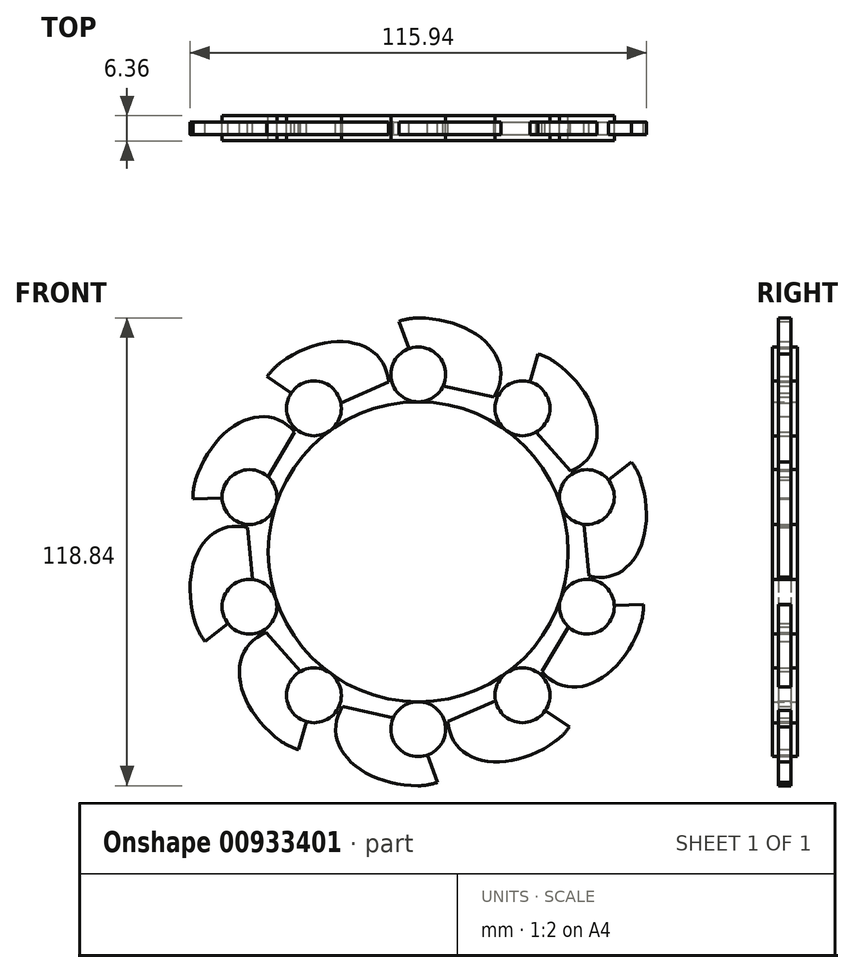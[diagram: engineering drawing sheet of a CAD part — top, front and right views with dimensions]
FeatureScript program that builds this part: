
annotation { "Feature Type Name" : "Feature", "Feature Type Description" : "" }
export const myFeature = defineFeature(function(context is Context, id is Id, definition is map)
    precondition{}
    {
        {
            var Q0;
            Q0=qCreatedBy(makeId("Front.planeOp"),FACE);
            var sketch = newSketch(context, id + "F0", { "sketchPlane" : qUnion([Q0])});
            skCircle(sketch, "E0", {"center": v(0, 0) * mm, "radius": 38.1 * mm});
            skCircle(sketch, "E1", {"center": v(0, 45.06) * mm, "radius": 6.96 * mm});
            skPoint(sketch, "E1.first.point", {"position": v(0.3, 38.1) * mm});
            skPoint(sketch, "E1.second.point", {"position": v(0, 52.02) * mm});
            skPoint(sketch, "E1.third.point", {"position": v(6.89, 46.1) * mm});
            skEllipticalArc(sketch, "E2", {});
            skArc(sketch, "E3", {"start": v(0, 59.42) * mm, "mid": v(-2.5, 59.2) * mm, "end": v(-4.91, 58.55) * mm});
            skPoint(sketch, "E3.second.point", {"position": v(0, 59.42) * mm});
            skLineSegment(sketch, "E4", {"start": v(19.23, 39.33) * mm, "end": v(6.33, 42.15) * mm});
            skLineSegment(sketch, "E5", {"start": v(-4.91, 58.55) * mm, "end": v(-2.38, 51.6) * mm});
            skEllipticalArc(sketch, "E6.1.0", {});
            skPoint(sketch, "E6.1.1", {"position": v(-34.93, 48.07) * mm});
            skLineSegment(sketch, "E6.1.2", {"start": v(-38.4, 44.48) * mm, "end": v(-32.26, 40.35) * mm});
            skArc(sketch, "E6.1.3", {"start": v(-34.93, 48.07) * mm, "mid": v(-36.82, 46.43) * mm, "end": v(-38.4, 44.48) * mm});
            skCircle(sketch, "E6.1.4", {"center": v(-26.49, 36.46) * mm, "radius": 6.96 * mm});
            skLineSegment(sketch, "E6.1.5", {"start": v(-7.56, 43.12) * mm, "end": v(-19.66, 37.82) * mm});
            skEllipticalArc(sketch, "E6.2.0", {});
            skPoint(sketch, "E6.2.1", {"position": v(-56.51, 18.36) * mm});
            skLineSegment(sketch, "E6.2.2", {"start": v(-57.2, 13.42) * mm, "end": v(-49.81, 13.68) * mm});
            skArc(sketch, "E6.2.3", {"start": v(-56.51, 18.36) * mm, "mid": v(-57.08, 15.92) * mm, "end": v(-57.2, 13.42) * mm});
            skCircle(sketch, "E6.2.4", {"center": v(-42.86, 13.92) * mm, "radius": 6.96 * mm});
            skLineSegment(sketch, "E6.2.5", {"start": v(-31.46, 30.44) * mm, "end": v(-38.14, 19.04) * mm});
            skEllipticalArc(sketch, "E6.3.0", {});
            skPoint(sketch, "E6.3.1", {"position": v(-56.51, -18.36) * mm});
            skLineSegment(sketch, "E6.3.2", {"start": v(-54.17, -22.77) * mm, "end": v(-48.34, -18.21) * mm});
            skArc(sketch, "E6.3.3", {"start": v(-56.51, -18.36) * mm, "mid": v(-55.53, -20.67) * mm, "end": v(-54.17, -22.77) * mm});
            skCircle(sketch, "E6.3.4", {"center": v(-42.86, -13.92) * mm, "radius": 6.96 * mm});
            skLineSegment(sketch, "E6.3.5", {"start": v(-43.35, 6.13) * mm, "end": v(-42.05, -7.01) * mm});
            skEllipticalArc(sketch, "E6.4.0", {});
            skPoint(sketch, "E6.4.1", {"position": v(-34.93, -48.07) * mm});
            skLineSegment(sketch, "E6.4.2", {"start": v(-30.44, -50.26) * mm, "end": v(-28.4, -43.15) * mm});
            skArc(sketch, "E6.4.3", {"start": v(-34.93, -48.07) * mm, "mid": v(-32.78, -49.36) * mm, "end": v(-30.44, -50.26) * mm});
            skCircle(sketch, "E6.4.4", {"center": v(-26.49, -36.46) * mm, "radius": 6.96 * mm});
            skLineSegment(sketch, "E6.4.5", {"start": v(-38.67, -20.52) * mm, "end": v(-29.9, -30.39) * mm});
            skEllipticalArc(sketch, "E6.5.0", {});
            skPoint(sketch, "E6.5.1", {"position": v(0, -59.42) * mm});
            skLineSegment(sketch, "E6.5.2", {"start": v(4.91, -58.55) * mm, "end": v(2.38, -51.6) * mm});
            skArc(sketch, "E6.5.3", {"start": v(0, -59.42) * mm, "mid": v(2.5, -59.2) * mm, "end": v(4.91, -58.55) * mm});
            skCircle(sketch, "E6.5.4", {"center": v(0, -45.06) * mm, "radius": 6.96 * mm});
            skLineSegment(sketch, "E6.5.5", {"start": v(-19.23, -39.33) * mm, "end": v(-6.33, -42.15) * mm});
            skEllipticalArc(sketch, "E6.6.0", {});
            skPoint(sketch, "E6.6.1", {"position": v(34.93, -48.07) * mm});
            skLineSegment(sketch, "E6.6.2", {"start": v(38.4, -44.48) * mm, "end": v(32.26, -40.35) * mm});
            skArc(sketch, "E6.6.3", {"start": v(34.93, -48.07) * mm, "mid": v(36.82, -46.43) * mm, "end": v(38.4, -44.48) * mm});
            skCircle(sketch, "E6.6.4", {"center": v(26.49, -36.46) * mm, "radius": 6.96 * mm});
            skLineSegment(sketch, "E6.6.5", {"start": v(7.56, -43.12) * mm, "end": v(19.66, -37.82) * mm});
            skEllipticalArc(sketch, "E6.7.0", {});
            skPoint(sketch, "E6.7.1", {"position": v(56.51, -18.36) * mm});
            skLineSegment(sketch, "E6.7.2", {"start": v(57.2, -13.42) * mm, "end": v(49.81, -13.68) * mm});
            skArc(sketch, "E6.7.3", {"start": v(56.51, -18.36) * mm, "mid": v(57.08, -15.92) * mm, "end": v(57.2, -13.42) * mm});
            skCircle(sketch, "E6.7.4", {"center": v(42.86, -13.92) * mm, "radius": 6.96 * mm});
            skLineSegment(sketch, "E6.7.5", {"start": v(31.46, -30.44) * mm, "end": v(38.14, -19.04) * mm});
            skEllipticalArc(sketch, "E6.8.0", {});
            skPoint(sketch, "E6.8.1", {"position": v(56.51, 18.36) * mm});
            skLineSegment(sketch, "E6.8.2", {"start": v(54.17, 22.77) * mm, "end": v(48.34, 18.21) * mm});
            skArc(sketch, "E6.8.3", {"start": v(56.51, 18.36) * mm, "mid": v(55.53, 20.67) * mm, "end": v(54.17, 22.77) * mm});
            skCircle(sketch, "E6.8.4", {"center": v(42.86, 13.92) * mm, "radius": 6.96 * mm});
            skLineSegment(sketch, "E6.8.5", {"start": v(43.35, -6.13) * mm, "end": v(42.05, 7.01) * mm});
            skEllipticalArc(sketch, "E6.9.0", {});
            skPoint(sketch, "E6.9.1", {"position": v(34.93, 48.07) * mm});
            skLineSegment(sketch, "E6.9.2", {"start": v(30.44, 50.26) * mm, "end": v(28.4, 43.15) * mm});
            skArc(sketch, "E6.9.3", {"start": v(34.93, 48.07) * mm, "mid": v(32.78, 49.36) * mm, "end": v(30.44, 50.26) * mm});
            skCircle(sketch, "E6.9.4", {"center": v(26.49, 36.46) * mm, "radius": 6.96 * mm});
            skLineSegment(sketch, "E6.9.5", {"start": v(38.67, 20.52) * mm, "end": v(29.9, 30.39) * mm});
            const initialGuessF0  = {"E2": [-6.830472484595004e-10, 0.04506209631672507, 0, 1, 0.014359558473914742, 0.020969135483775932, 4.301780921279478, 6.283185307179586], "E6.1.0": [-0.026486836204950803, 0.036456001320906206, -0.5877852522924731, 0.8090169943749475, 0.014359558473914742, 0.020969135483775932, 4.301780921279478, 6.283185307179586], "E6.2.0": [-0.04285660055101442, 0.013924952914412236, -0.9510565162951538, 0.3090169943749475, 0.014359558473914742, 0.020969135483775932, 4.301780921279478, 6.283185307179586], "E6.3.0": [-0.042856600128868015, -0.013924954213645303, -0.9510565162951536, -0.30901699437494734, 0.014359558473914742, 0.020969135483775932, 4.301780921279478, 6.283185307179586], "E6.4.0": [-0.026486835099757144, -0.0364560021238764, -0.5877852522924732, -0.8090169943749473, 0.014359558473914742, 0.020969135483775932, 4.301780921279478, 6.283185307179586], "E6.5.0": [6.830472429409852e-10, -0.04506209631672507, 0, -1, 0.014359558473914742, 0.020969135483775932, 4.301780921279478, 6.283185307179586], "E6.6.0": [0.0264868362049508, -0.03645600132090621, 0.587785252292473, -0.8090169943749476, 0.014359558473914742, 0.020969135483775932, 4.301780921279478, 6.283185307179586], "E6.7.0": [0.04285660055101442, -0.013924952914412241, 0.9510565162951535, -0.30901699437494756, 0.014359558473914742, 0.020969135483775932, 4.301780921279478, 6.283185307179586], "E6.8.0": [0.042856600128868015, 0.013924954213645297, 0.9510565162951536, 0.30901699437494723, 0.014359558473914742, 0.020969135483775932, 4.301780921279478, 6.283185307179586], "E6.9.0": [0.026486835099757147, 0.0364560021238764, 0.5877852522924734, 0.8090169943749473, 0.014359558473914742, 0.020969135483775932, 4.301780921279478, 6.283185307179586]};
            skSetInitialGuess(sketch, initialGuessF0);
            skSolve(sketch);
        }
        {
            var Q0;
            {var subQ0=sQuery(id+"F0.wireOp",EDGE,"E0");var subQ4=makeQuery(id+"F0.imprint","INTERSECT",VERTEX,{"derivedFrom":[subQ0,sQuery(id+"F0.wireOp",EDGE,"E6.9.4")]});Q0=makeQuery(id+"F0.imprint","IMPRINT",FACE,{"disambiguationData":[TD([[makeQuery(id+"F0.imprint","IMPRINT",EDGE,{"disambiguationData":[TD([[subQ4,1.0]])],"derivedFrom":subQ0}),1.0]])]});}
            extrude(context, id + "F1", {"entities" : qUnion([Q0]), "endBound" : BoundingType.SYMMETRIC, "depth" : 6.35 * mm, "offsetDistance" : 25.4 * mm});
        }
        {
            var Q0;
            {var subQ0=sQuery(id+"F0.wireOp",EDGE,"E6.8.4");var subQ1=makeQuery(id+"F0.imprint","INTERSECT",VERTEX,{"derivedFrom":[sQuery(id+"F0.wireOp",EDGE,"E6.8.2"),subQ0]});Q0=makeQuery(id+"F0.imprint","IMPRINT",FACE,{"disambiguationData":[TD([[makeQuery(id+"F0.imprint","IMPRINT",EDGE,{"disambiguationData":[TD([[subQ1,-1.0]])],"derivedFrom":subQ0}),1.0]])]});}
            var Q1;
            {var subQ0=sQuery(id+"F0.wireOp",EDGE,"E6.7.4");var subQ1=makeQuery(id+"F0.imprint","INTERSECT",VERTEX,{"derivedFrom":[sQuery(id+"F0.wireOp",EDGE,"E6.7.2"),subQ0]});Q1=makeQuery(id+"F0.imprint","IMPRINT",FACE,{"disambiguationData":[TD([[makeQuery(id+"F0.imprint","IMPRINT",EDGE,{"disambiguationData":[TD([[subQ1,-1.0]])],"derivedFrom":subQ0}),1.0]])]});}
            var Q2;
            {var subQ0=sQuery(id+"F0.wireOp",EDGE,"E6.9.4");var subQ1=makeQuery(id+"F0.imprint","INTERSECT",VERTEX,{"derivedFrom":[sQuery(id+"F0.wireOp",EDGE,"E6.9.2"),subQ0]});Q2=makeQuery(id+"F0.imprint","IMPRINT",FACE,{"disambiguationData":[TD([[makeQuery(id+"F0.imprint","IMPRINT",EDGE,{"disambiguationData":[TD([[subQ1,-1.0]])],"derivedFrom":subQ0}),1.0]])]});}
            var Q3;
            {var subQ0=sQuery(id+"F0.wireOp",EDGE,"E1");var subQ1=makeQuery(id+"F0.imprint","INTERSECT",VERTEX,{"derivedFrom":[subQ0,sQuery(id+"F0.wireOp",EDGE,"E5")]});Q3=makeQuery(id+"F0.imprint","IMPRINT",FACE,{"disambiguationData":[TD([[makeQuery(id+"F0.imprint","IMPRINT",EDGE,{"disambiguationData":[TD([[subQ1,-1.0]])],"derivedFrom":subQ0}),1.0]])]});}
            var Q4;
            {var subQ0=sQuery(id+"F0.wireOp",EDGE,"E6.1.4");var subQ1=makeQuery(id+"F0.imprint","INTERSECT",VERTEX,{"derivedFrom":[sQuery(id+"F0.wireOp",EDGE,"E6.1.2"),subQ0]});Q4=makeQuery(id+"F0.imprint","IMPRINT",FACE,{"disambiguationData":[TD([[makeQuery(id+"F0.imprint","IMPRINT",EDGE,{"disambiguationData":[TD([[subQ1,-1.0]])],"derivedFrom":subQ0}),1.0]])]});}
            var Q5;
            {var subQ0=sQuery(id+"F0.wireOp",EDGE,"E6.2.4");var subQ1=makeQuery(id+"F0.imprint","INTERSECT",VERTEX,{"derivedFrom":[sQuery(id+"F0.wireOp",EDGE,"E6.2.2"),subQ0]});Q5=makeQuery(id+"F0.imprint","IMPRINT",FACE,{"disambiguationData":[TD([[makeQuery(id+"F0.imprint","IMPRINT",EDGE,{"disambiguationData":[TD([[subQ1,-1.0]])],"derivedFrom":subQ0}),1.0]])]});}
            var Q6;
            {var subQ0=sQuery(id+"F0.wireOp",EDGE,"E6.3.4");var subQ1=makeQuery(id+"F0.imprint","INTERSECT",VERTEX,{"derivedFrom":[sQuery(id+"F0.wireOp",EDGE,"E6.3.2"),subQ0]});Q6=makeQuery(id+"F0.imprint","IMPRINT",FACE,{"disambiguationData":[TD([[makeQuery(id+"F0.imprint","IMPRINT",EDGE,{"disambiguationData":[TD([[subQ1,-1.0]])],"derivedFrom":subQ0}),1.0]])]});}
            var Q7;
            {var subQ0=sQuery(id+"F0.wireOp",EDGE,"E6.4.4");var subQ1=makeQuery(id+"F0.imprint","INTERSECT",VERTEX,{"derivedFrom":[sQuery(id+"F0.wireOp",EDGE,"E6.4.2"),subQ0]});Q7=makeQuery(id+"F0.imprint","IMPRINT",FACE,{"disambiguationData":[TD([[makeQuery(id+"F0.imprint","IMPRINT",EDGE,{"disambiguationData":[TD([[subQ1,-1.0]])],"derivedFrom":subQ0}),1.0]])]});}
            var Q8;
            {var subQ0=sQuery(id+"F0.wireOp",EDGE,"E6.5.4");var subQ1=makeQuery(id+"F0.imprint","INTERSECT",VERTEX,{"derivedFrom":[sQuery(id+"F0.wireOp",EDGE,"E6.5.2"),subQ0]});Q8=makeQuery(id+"F0.imprint","IMPRINT",FACE,{"disambiguationData":[TD([[makeQuery(id+"F0.imprint","IMPRINT",EDGE,{"disambiguationData":[TD([[subQ1,-1.0]])],"derivedFrom":subQ0}),1.0]])]});}
            var Q9;
            {var subQ0=sQuery(id+"F0.wireOp",EDGE,"E6.6.4");var subQ1=makeQuery(id+"F0.imprint","INTERSECT",VERTEX,{"derivedFrom":[sQuery(id+"F0.wireOp",EDGE,"E6.6.2"),subQ0]});Q9=makeQuery(id+"F0.imprint","IMPRINT",FACE,{"disambiguationData":[TD([[makeQuery(id+"F0.imprint","IMPRINT",EDGE,{"disambiguationData":[TD([[subQ1,-1.0]])],"derivedFrom":subQ0}),1.0]])]});}
            extrude(context, id + "F2", {"entities" : qUnion([Q0, Q1, Q2, Q3, Q4, Q5, Q6, Q7, Q8, Q9]), "endBound" : BoundingType.SYMMETRIC, "depth" : 6.35 * mm, "offsetDistance" : 25.4 * mm});
        }
        {
            var Q0;
            Q0=makeQuery(id+"F0.imprint","IMPRINT",FACE,{"disambiguationData":[TD([[makeQuery(id+"F0.imprint","IMPRINT",EDGE,{"derivedFrom":sQuery(id+"F0.wireOp",EDGE,"E2")}),1.0]])]});
            var Q1;
            Q1=makeQuery(id+"F0.imprint","IMPRINT",FACE,{"disambiguationData":[TD([[makeQuery(id+"F0.imprint","IMPRINT",EDGE,{"derivedFrom":sQuery(id+"F0.wireOp",EDGE,"E6.1.0")}),1.0]])]});
            var Q2;
            Q2=makeQuery(id+"F0.imprint","IMPRINT",FACE,{"disambiguationData":[TD([[makeQuery(id+"F0.imprint","IMPRINT",EDGE,{"derivedFrom":sQuery(id+"F0.wireOp",EDGE,"E6.2.0")}),1.0]])]});
            var Q3;
            Q3=makeQuery(id+"F0.imprint","IMPRINT",FACE,{"disambiguationData":[TD([[makeQuery(id+"F0.imprint","IMPRINT",EDGE,{"derivedFrom":sQuery(id+"F0.wireOp",EDGE,"E6.3.0")}),1.0]])]});
            var Q4;
            Q4=makeQuery(id+"F0.imprint","IMPRINT",FACE,{"disambiguationData":[TD([[makeQuery(id+"F0.imprint","IMPRINT",EDGE,{"derivedFrom":sQuery(id+"F0.wireOp",EDGE,"E6.4.0")}),1.0]])]});
            var Q5;
            Q5=makeQuery(id+"F0.imprint","IMPRINT",FACE,{"disambiguationData":[TD([[makeQuery(id+"F0.imprint","IMPRINT",EDGE,{"derivedFrom":sQuery(id+"F0.wireOp",EDGE,"E6.5.0")}),1.0]])]});
            var Q6;
            Q6=makeQuery(id+"F0.imprint","IMPRINT",FACE,{"disambiguationData":[TD([[makeQuery(id+"F0.imprint","IMPRINT",EDGE,{"derivedFrom":sQuery(id+"F0.wireOp",EDGE,"E6.6.0")}),1.0]])]});
            var Q7;
            Q7=makeQuery(id+"F0.imprint","IMPRINT",FACE,{"disambiguationData":[TD([[makeQuery(id+"F0.imprint","IMPRINT",EDGE,{"derivedFrom":sQuery(id+"F0.wireOp",EDGE,"E6.7.0")}),1.0]])]});
            var Q8;
            Q8=makeQuery(id+"F0.imprint","IMPRINT",FACE,{"disambiguationData":[TD([[makeQuery(id+"F0.imprint","IMPRINT",EDGE,{"derivedFrom":sQuery(id+"F0.wireOp",EDGE,"E6.8.0")}),1.0]])]});
            var Q9;
            Q9=makeQuery(id+"F0.imprint","IMPRINT",FACE,{"disambiguationData":[TD([[makeQuery(id+"F0.imprint","IMPRINT",EDGE,{"derivedFrom":sQuery(id+"F0.wireOp",EDGE,"E6.9.0")}),1.0]])]});
            extrude(context, id + "F3", {"entities" : qUnion([Q0, Q1, Q2, Q3, Q4, Q5, Q6, Q7, Q8, Q9]), "endBound" : BoundingType.SYMMETRIC, "depth" : 3.17 * mm, "offsetDistance" : 25.4 * mm});
        }
    });
